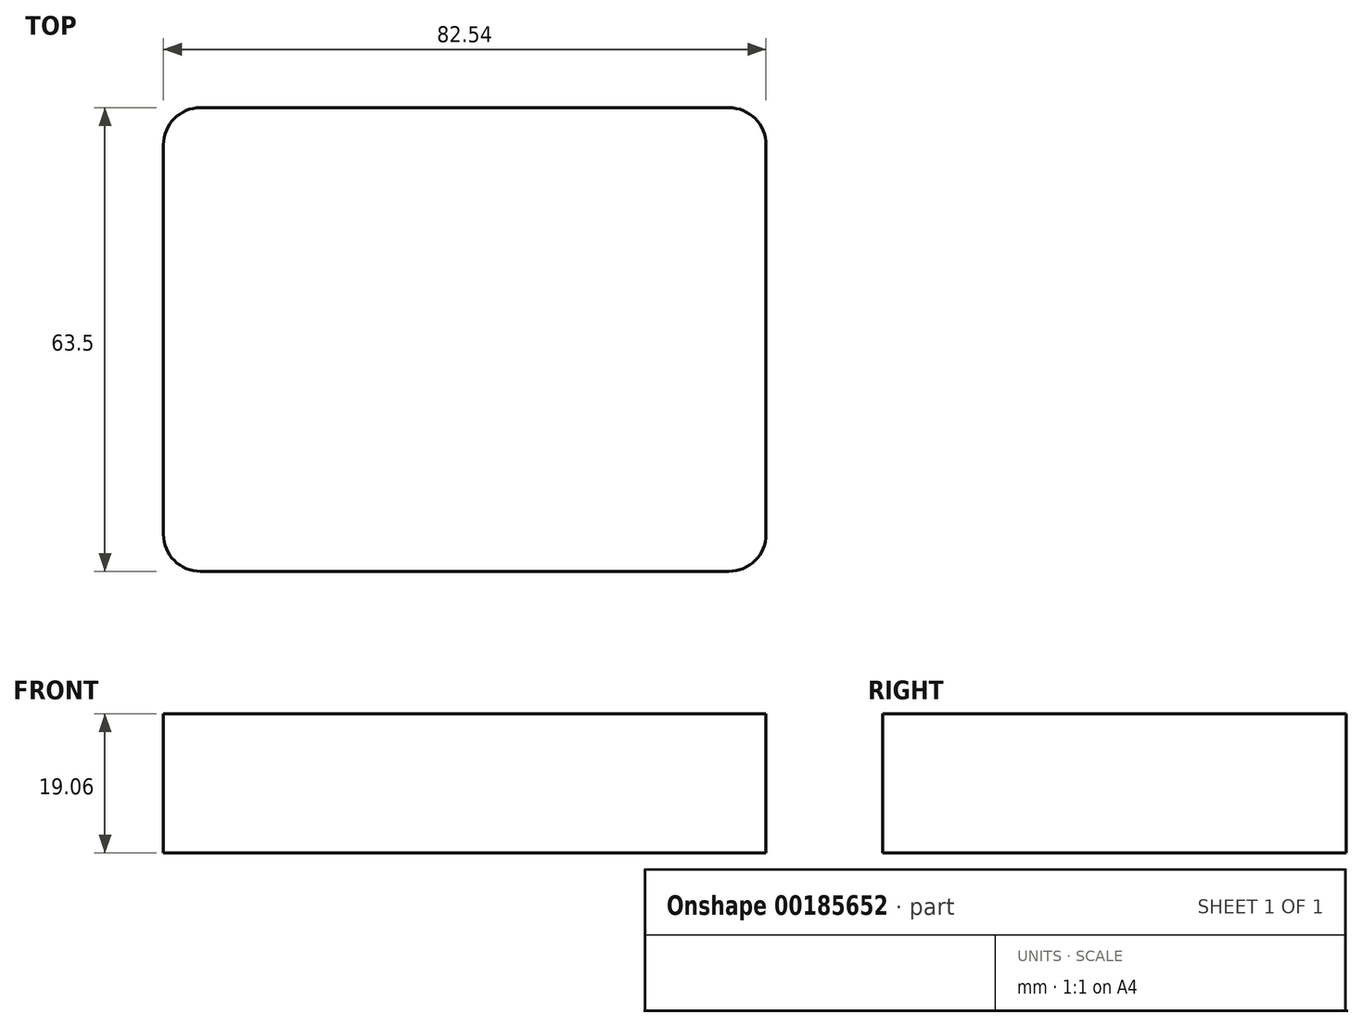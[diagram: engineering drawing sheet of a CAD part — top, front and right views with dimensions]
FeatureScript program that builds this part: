
annotation { "Feature Type Name" : "Feature", "Feature Type Description" : "" }
export const myFeature = defineFeature(function(context is Context, id is Id, definition is map)
    precondition{}
    {
        {
            var Q0;
            Q0=qCreatedBy(makeId("Front.planeOp"),FACE);
            var sketch = newSketch(context, id + "F0", { "sketchPlane" : qUnion([Q0])});
            skLineSegment(sketch, "E0.bottom", {"start": v(-41.28, -9.53) * mm, "end": v(41.28, -9.53) * mm});
            skLineSegment(sketch, "E0.top", {"start": v(-41.28, 9.53) * mm, "end": v(41.28, 9.53) * mm});
            skLineSegment(sketch, "E0.left", {"start": v(-41.28, -9.53) * mm, "end": v(-41.28, 9.53) * mm});
            skLineSegment(sketch, "E0.right", {"start": v(41.28, -9.53) * mm, "end": v(41.28, 9.52) * mm});
            skPoint(sketch, "E0.middle", {"position": v(0, 0) * mm});
            skLineSegment(sketch, "E1.bottom", {"start": v(65.28, 45.92) * mm, "end": v(116.08, 45.92) * mm});
            skLineSegment(sketch, "E1.top", {"start": v(65.28, 74.5) * mm, "end": v(116.08, 74.5) * mm});
            skLineSegment(sketch, "E1.left", {"start": v(65.28, 45.92) * mm, "end": v(65.28, 74.5) * mm});
            skLineSegment(sketch, "E1.right", {"start": v(116.08, 45.92) * mm, "end": v(116.08, 74.5) * mm});
            skPoint(sketch, "E1.middle", {"position": v(90.68, 60.2) * mm});
            skLineSegment(sketch, "E2", {"start": v(41.28, 9.52) * mm, "end": v(41.28, 35.85) * mm});
            skArc(sketch, "E3", {"start": v(41.27, 35.85) * mm, "mid": v(45.92, 47.08) * mm, "end": v(57.15, 51.73) * mm});
            skLineSegment(sketch, "E4", {"start": v(57.15, 51.73) * mm, "end": v(86.4, 51.73) * mm});
            skSolve(sketch);
        }
        {
            var Q0;
            Q0=makeQuery(id+"F0.imprint","IMPRINT",FACE,{"disambiguationData":[TD([[makeQuery(id+"F0.imprint","IMPRINT",EDGE,{"derivedFrom":sQuery(id+"F0.wireOp",EDGE,"E0.bottom")}),1.0]])]});
            extrude(context, id + "F1", {"entities" : qUnion([Q0]), "endBound" : BoundingType.SYMMETRIC, "depth" : 63.5 * mm});
        }
        {
            var Q0;
            Q0=makeQuery(id+"F1.opExtrude","CAP_EDGE",EDGE,{"disambiguationData":[OSD([sQuery(id+"F0.wireOp",EDGE,"E0.left")])],"isStart":false});
            var Q1;
            Q1=makeQuery(id+"F1.opExtrude","CAP_EDGE",EDGE,{"disambiguationData":[OSD([sQuery(id+"F0.wireOp",EDGE,"E0.right")])],"isStart":false});
            var Q2;
            Q2=makeQuery(id+"F1.opExtrude","CAP_EDGE",EDGE,{"disambiguationData":[OSD([sQuery(id+"F0.wireOp",EDGE,"E0.right")])],"isStart":true});
            var Q3;
            Q3=makeQuery(id+"F1.opExtrude","CAP_EDGE",EDGE,{"disambiguationData":[OSD([sQuery(id+"F0.wireOp",EDGE,"E0.left")])],"isStart":true});
            fillet(context, id + "F2", {"entities" : qUnion([Q0, Q1, Q2, Q3]), "radius" : 5.08 * mm, "tangentPropagation" : true, "allowEdgeOverflow" : false});
        }
    });
